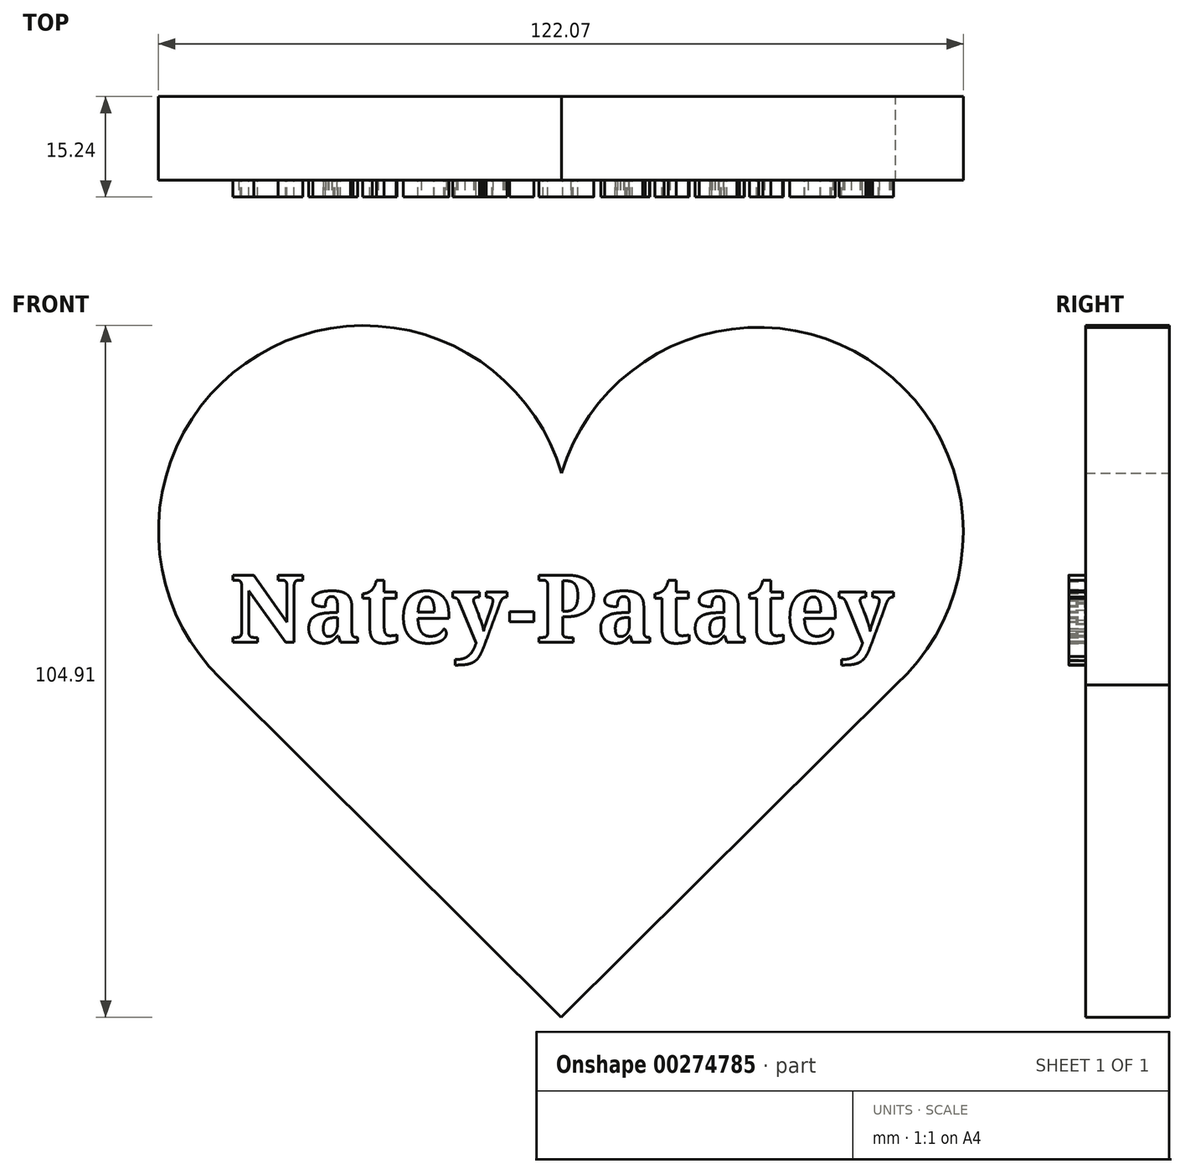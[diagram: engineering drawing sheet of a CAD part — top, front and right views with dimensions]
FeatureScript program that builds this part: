
annotation { "Feature Type Name" : "Feature", "Feature Type Description" : "" }
export const myFeature = defineFeature(function(context is Context, id is Id, definition is map)
    precondition{}
    {
        {
            var Q0;
            Q0=qCreatedBy(makeId("Front.planeOp"),FACE);
            var sketch = newSketch(context, id + "F0", { "sketchPlane" : qUnion([Q0])});
            skArc(sketch, "E0", {"start": v(-0.02, 18.95) * mm, "mid": v(-0.01, 18.97) * mm, "end": v(0, 18.98) * mm});
            skArc(sketch, "E1.MirrorC", {"start": v(0, 18.95) * mm, "mid": v(0, 18.97) * mm, "end": v(0, 18.98) * mm});
            skLineSegment(sketch, "E2", {"start": v(0, -45.71) * mm, "end": v(-52.04, 6.01) * mm});
            skLineSegment(sketch, "E3.MirrorCS", {"start": v(0, -45.71) * mm, "end": v(52.04, 6.01) * mm});
            skPoint(sketch, "E4", {"position": v(0, 18.95) * mm});
            skPoint(sketch, "E5", {"position": v(-0.02, 18.95) * mm});
            skPoint(sketch, "E6.orphan", {"position": v(0, 55.04) * mm});
            skPoint(sketch, "E7.end.orphan", {"position": v(0, -17.15) * mm});
            skPoint(sketch, "E8", {"position": v(0, 36.66) * mm});
            skArc(sketch, "E9.trimOffspring", {"start": v(0, 36.66) * mm, "mid": v(46.44, 54.15) * mm, "end": v(50.72, 4.7) * mm});
            skArc(sketch, "E10.trimOffspring", {"start": v(0.05, 36.82) * mm, "mid": v(-45.96, 54.75) * mm, "end": v(-51.74, 5.72) * mm});
            skSolve(sketch);
        }
        {
            var Q0;
            Q0 = qSketchRegion(id + "F0", true);
            extrude(context, id + "F1", {"entities" : qUnion([Q0]), "depth" : 12.7 * mm});
        }
        {
            var Q0;
            Q0=makeQuery(id+"F1.opExtrude","CAP_FACE",FACE,{"disambiguationData":[OSD([sQuery(id+"F0.wireOp",EDGE,"E2"),sQuery(id+"F0.wireOp",EDGE,"E3.MirrorCS"),sQuery(id+"F0.wireOp",EDGE,"E9.trimOffspring"),sQuery(id+"F0.wireOp",EDGE,"E10.trimOffspring")])],"isStart":false});
            var sketch = newSketch(context, id + "F2", { "sketchPlane" : qUnion([Q0])});
            skText(sketch, "E11", { "text": "Natey-Patatey", "fontName": "NotoSerif-Bold.ttf"});
            const initialGuessF2  = {"E11": [-0.0502, 0.01113, 1, 0, 0.01028]};
            skSetInitialGuess(sketch, initialGuessF2);
            skSolve(sketch);
        }
        {
            var Q0;
            Q0 = qSketchRegion(id + "F2", true);
            extrude(context, id + "F3", {"entities" : qUnion([Q0]), "operationType" : NewBodyOperationType.ADD, "depth" : 2.54 * mm});
        }
    });
